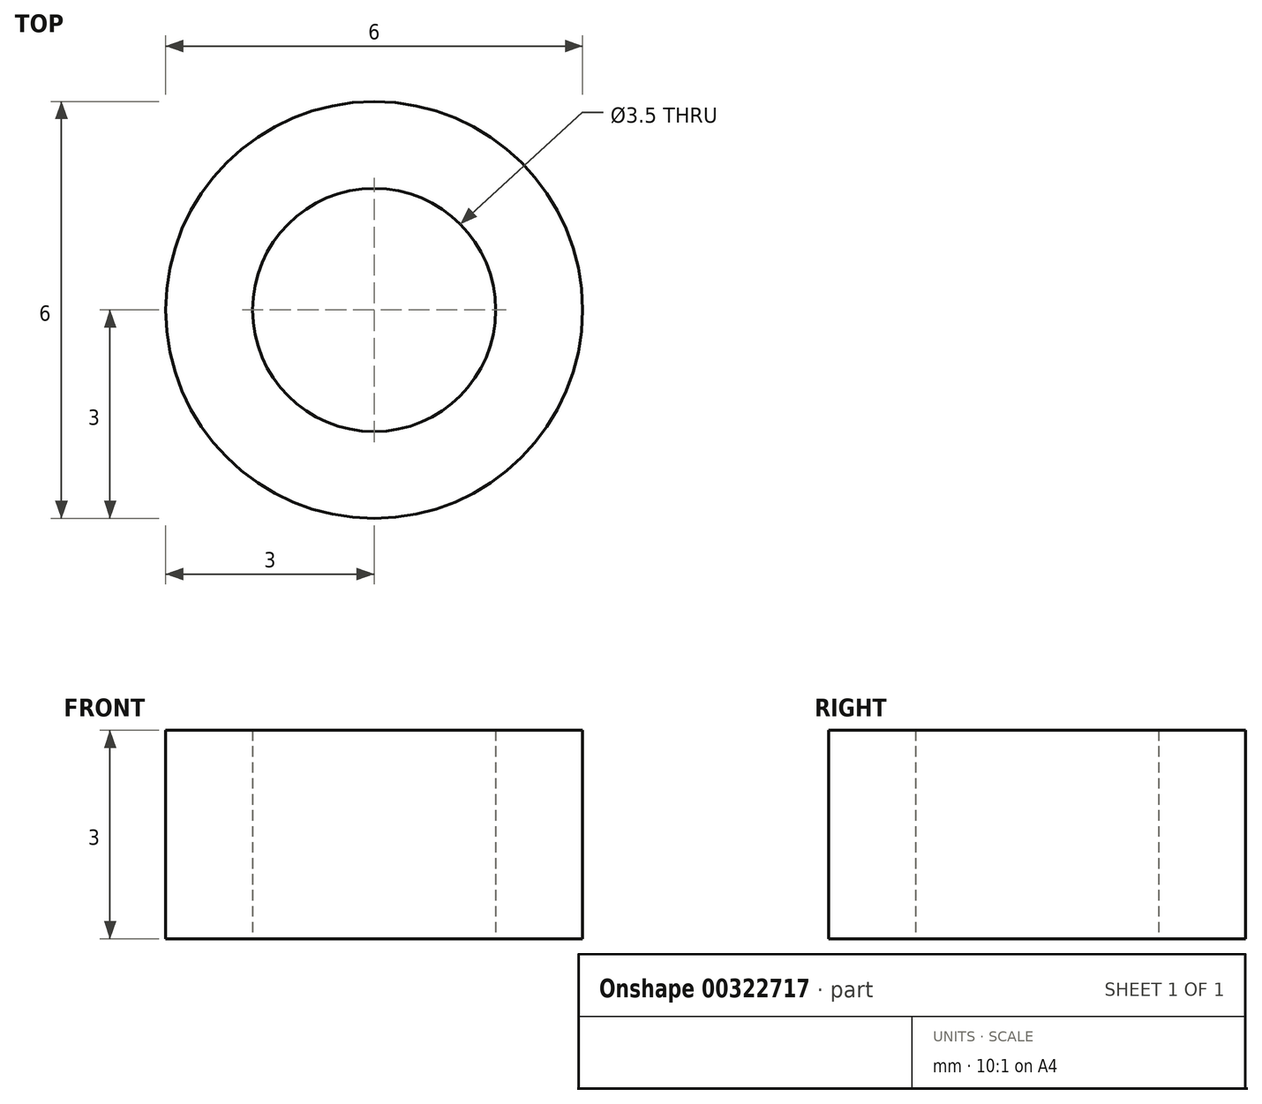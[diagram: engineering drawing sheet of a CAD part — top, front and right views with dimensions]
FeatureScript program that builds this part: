
annotation { "Feature Type Name" : "Feature", "Feature Type Description" : "" }
export const myFeature = defineFeature(function(context is Context, id is Id, definition is map)
    precondition{}
    {
        {
            var Q0;
            Q0=qCreatedBy(makeId("Top.planeOp"),FACE);
            var sketch = newSketch(context, id + "F0", { "sketchPlane" : qUnion([Q0])});
            skCircle(sketch, "E0", {"center": v(0, 0) * mm, "radius": 3 * mm});
            skCircle(sketch, "E1", {"center": v(0, 0) * mm, "radius": 1.75 * mm});
            skSolve(sketch);
        }
        {
            var Q0;
            Q0=makeQuery(id+"F0.imprint","IMPRINT",FACE,{"disambiguationData":[TD([[makeQuery(id+"F0.imprint","IMPRINT",EDGE,{"derivedFrom":sQuery(id+"F0.wireOp",EDGE,"E0")}),1.0]])]});
            extrude(context, id + "F1", {"entities" : qUnion([Q0]), "depth" : 3 * mm, "offsetDistance" : 25 * mm});
        }
    });
